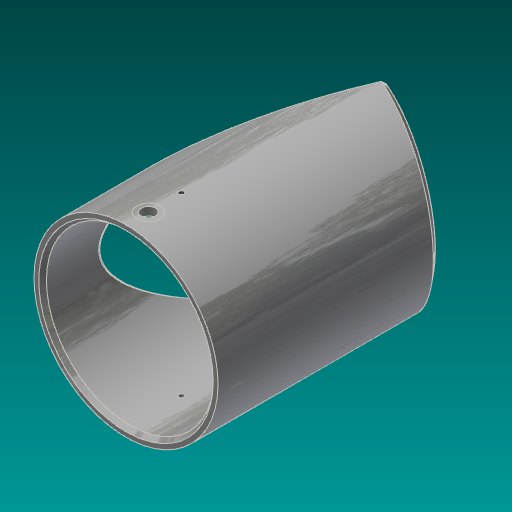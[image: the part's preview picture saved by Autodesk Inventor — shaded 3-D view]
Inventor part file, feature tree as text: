
AUTODESK INVENTOR PART (.ipt)
format: ipt  version: 2017.3 (Build 213256000, 256)  size: 458,752 bytes
history: native  units: in
note: dims shown in document units (in); Inventor stores cm internally (conversion verified against a paired STEP export)
features: other x19, loft x8, split x7, extrude x5, plane x4, sketch x3, hole x2, chamfer x1, pattern_circular x1
ambient origin geometry x8: Origin, YZ Plane, XZ Plane, XY Plane, X Axis, Y Axis, Z Axis, Center Point
bodies: Solid1 (feature_tree)
feature tree (50):
  sketch  "Sketch1"  dims[d0=30.25in d1=33.25in]
  extrude  "Extrusion1"  Depth=33.25in
  sketch  "Sketch2"  dims[d2=47.0236in d3=0.0in d4=22.5deg]
  extrude  "Extrusion2"  TaperAngle=22.5deg  [1 undecoded]
  split  "Split1"
  split  "Split2"
  plane  "Work Plane1"
  plane  "Work Plane2"
  split  "Split3"
  split  "Split4"
  split  "Split5"
  loft  "Loft5"
  loft  "Loft6"
  loft  "Loft7"
  loft  "Loft8"
  loft  "Loft9"
  loft  "Loft10"
  loft  "Loft11"
  plane  "Work Plane3"
  split  "Split6"
  loft  "Loft13"
  chamfer  "Chamfer1"  [1 undecoded]
  plane  "Work Plane4"
  sketch  "Sketch4"  dims[d5=60.0079in d6=0.0in d7=30.375in d8=0.0in d9=0.0in d10=0.0469in d11=0.0469in d13=1.103in d14=1.103in d15=60.0079in d16=0.0in d18=-1.103in d19=-1.103in d36=0.0in d37=90.0deg d38=0.0in d39=90.0deg d40=0.0in d41=90.0deg d42=0.0in d43=90.0deg d44=0.0in d45=90.0deg d46=0.0in d47=90.0deg d48=0.0in d49=90.0deg d50=0.0in d51=90.0deg d52=0.0in d53=90.0deg d54=0.0in d55=90.0deg d56=0.0in d57=90.0deg d58=0.0in d59=90.0deg d60=0.0in d61=90.0deg d62=0.0in d63=90.0deg d68=0.0in d69=90.0deg d70=0.0in d71=90.0deg d72=0.75in d73=0.125in d74=0.2749in d75=4.0in d76=4.125in d77=2.5625in d78=0.75in d79=0.375in d80=0.25in d81=0.5635in d82=2.0in d83=0.8108in d84=1.0in d85=0.0in d86=6.0in d87=0.891in d88=0.553in d89=0.0246in d90=0.897in d91=0.375in d92=0.25in d93=0.5635in d94=2.0in d95=0.8108in d96=0.7874in d97=360.0deg]
  hole  "Hole1"  [1 undecoded]
  split  "Split7"
  hole  "Hole2"  [1 undecoded]
  pattern_circular  "Circular Pattern1"  Angle=90.0deg  [1 undecoded]
  other  "Srf1"
  other  "Srf2"
  other  "Edges9"
  other  "Edges10"
  other  "Edges11"
  other  "Edges12"
  other  "Edges13"
  other  "Edges14"
  other  "Edges15"
  other  "Edges16"
  other  "Edges17"
  other  "Edges18"
  other  "Edges19"
  other  "Edges20"
  other  "Edges21"
  other  "Edges22"
  other  "Edges25"
  other  "Edges26"
  other  "Srf3"
  extrude  "ExtrusionSrf1"  TaperAngle=0.0deg  [1 undecoded]
  extrude  "ExtrusionSrf2"  TaperAngle=0.0deg  [1 undecoded]
  extrude  "ExtrusionSrf3"  TaperAngle=0.0deg  [1 undecoded]
note: 8 required parameter values undecoded (feature->parameter linkage not recoverable at this tier; creation-order binding heuristic only, values carry confidence <= 0.55)
